# Revit family: Table-Teknion-JNTV-Navigate_Height_Adjustable_120-R2018
name_source: partatom
category: Furniture
revit_build: Autodesk Revit 2018 (Build: 20190510_1515(x64)
units: mm (PartAtom-declared; Revit-internal decimal feet)

## family parameters
Always vertical = No
Cut with Voids When Loaded = No
OmniClass Number = 23.40.20.00
OmniClass Title = General Furniture and Specialties
Room Calculation Point = No
Shared = Yes
Work Plane-Based = No

## types (6) — shared parameters
Assembly Code = E2020200
Manufacturer = Teknion
Manufacturer Fax = 416.661.4586
Part Number = JNTV
Product Documentation Link = https://www.teknion.com
Product Documentation Link 2 = https://www.teknion.com
Product Line = Expansion Cityline
Product Page URL = https://www.teknion.com
Series = Expansion Cityline
Sustainability Data = https://www.teknion.com
URL = www.teknion.com
Unit Weight URL = http://www.teknion.com
Warranty = http://www.teknion.com

## per-type parameters (varying)
| type | 23 Foot | 29 Foot | Actual Depth A | Actual Depth B | Depth | Description | L | Left 2Ds | Midsupport Inner | Model | R | Right 2Ds | S |
| 23" Depth, Standard Width Configuration | Yes | No | 14.045 " | 8.955 " | 23 " | Navigate Height-Adjustable Base - 120 , 23" Depth A, 23" Depth B, Standard Width Configuration | No | Table-Teknion-JNTV-Navigate_Height_Adjustable_120-Left2Ds-2018 : 23" Depth, Standard Width Configuration | 11.355 " | JNTVN_2323__S_ | No | Table-Teknion-JNTV-Navigate_Height_Adjustable_120-Right2Ds-2018 : 23" Depth, Standard Width Configuration | Yes |
| 29" Depth, Standard Width Configuration | No | Yes | 15.045 " | 13.955 " | 29 " | Navigate Height-Adjustable Base - 120 , 29" Depth A, 29" Depth B, Standard Width Configuration | No | Table-Teknion-JNTV-Navigate_Height_Adjustable_120-Left2Ds-2018 : 29" Depth, Standard Width Configuration | 10.778 " | JNTVN_2929__S_ | No | Table-Teknion-JNTV-Navigate_Height_Adjustable_120-Right2Ds-2018 : 29" Depth, Standard Width Configuration | Yes |
| 23" Depth, Standard - Recessed on Left | Yes | No | 14.045 " | 8.955 " | 23 " | Navigate Height-Adjustable Base - 120 , 23" Depth A, 23" Depth B, Standard - Recessed on Left Width Configuration | Yes | Table-Teknion-JNTV-Navigate_Height_Adjustable_120-Left2Ds-2018 : 23" Depth, Standard - Recessed on Left | 11.355 " | JNTVN_2323__L_ | No | Table-Teknion-JNTV-Navigate_Height_Adjustable_120-Right2Ds-2018 : 23" Depth, Standard Width Configuration | No |
| 23" Depth, Standard - Recessed on Right | Yes | No | 14.045 " | 8.955 " | 23 " | Navigate Height-Adjustable Base - 120 , 23" Depth A, 23" Depth B, Standard - Recessed on Right Width Configuration | No | Table-Teknion-JNTV-Navigate_Height_Adjustable_120-Left2Ds-2018 : 23" Depth, Standard Width Configuration | 11.355 " | JNTVN_2323__R_ | Yes | Table-Teknion-JNTV-Navigate_Height_Adjustable_120-Right2Ds-2018 : 23" Depth, Standard - Recessed on Right | No |
| 29" Depth, Standard - Recessed on Left | No | Yes | 15.045 " | 13.955 " | 29 " | Navigate Height-Adjustable Base - 120 , 29" Depth A, 29" Depth B, Standard - Recessed on Left | Yes | Table-Teknion-JNTV-Navigate_Height_Adjustable_120-Left2Ds-2018 : 29" Depth, Standard - Recessed on Left | 10.778 " | JNTVN_2929__L_ | No | Table-Teknion-JNTV-Navigate_Height_Adjustable_120-Right2Ds-2018 : 29" Depth, Standard Width Configuration | No |
| 29" Depth, Standard - Recessed on Right | No | Yes | 15.045 " | 13.955 " | 29 " | Navigate Height-Adjustable Base - 120 , 29" Depth A, 29" Depth B, Standard - Recessed on Right | No | Table-Teknion-JNTV-Navigate_Height_Adjustable_120-Left2Ds-2018 : 29" Depth, Standard Width Configuration | 10.778 " | JNTVN_2929__R_ | Yes | Table-Teknion-JNTV-Navigate_Height_Adjustable_120-Right2Ds-2018 : 29" Depth, Standard - Recessed on Right | No |

## geometry (parser evidence)
native form markers: Sweep x9
no freeform markers — native parametric forms only
